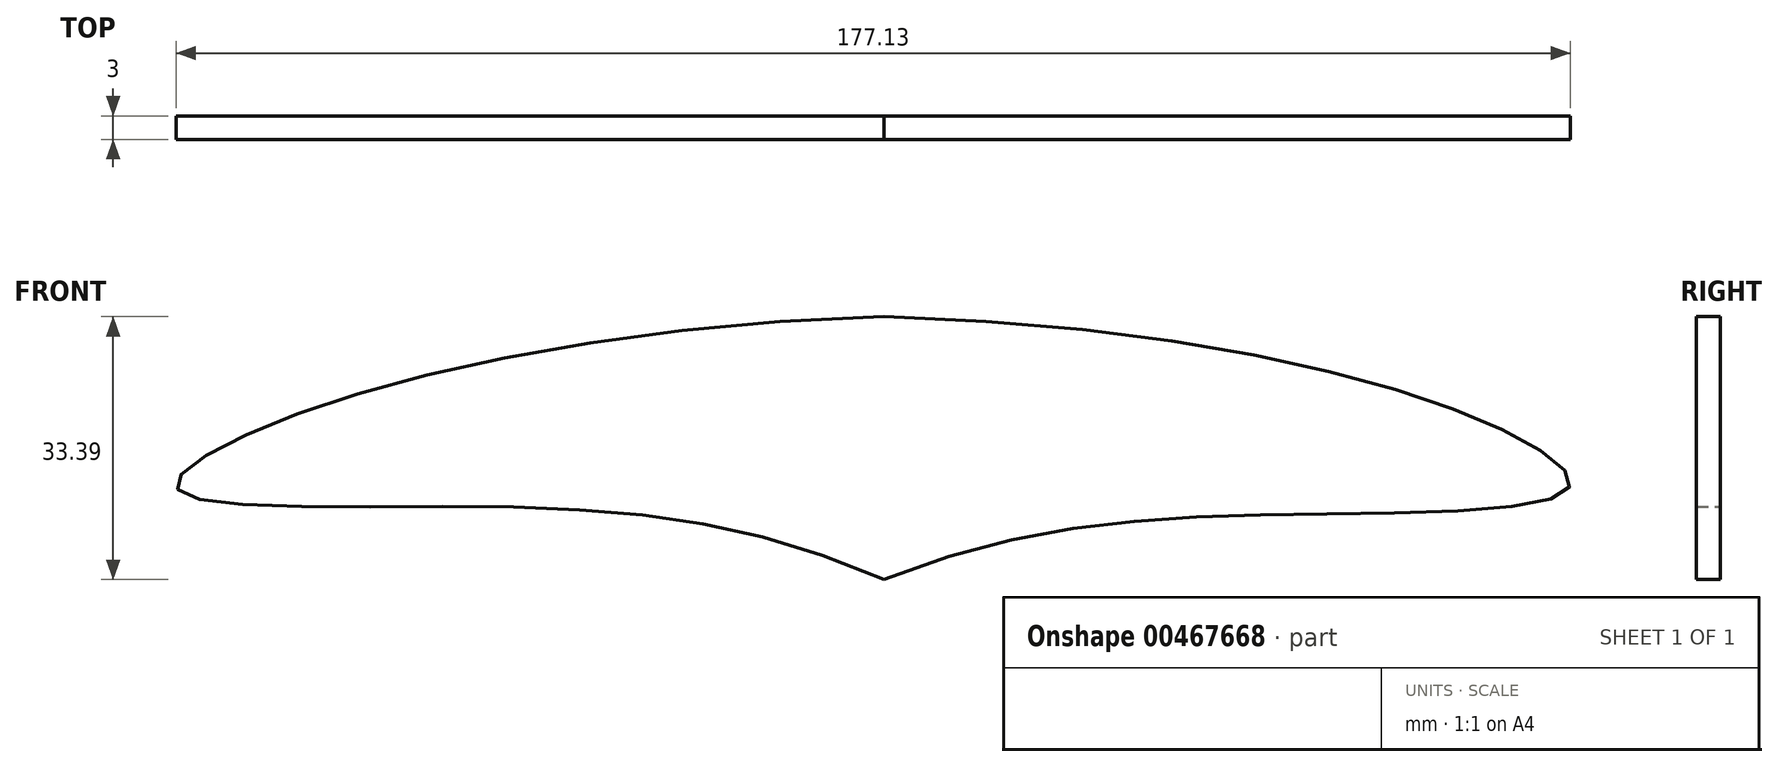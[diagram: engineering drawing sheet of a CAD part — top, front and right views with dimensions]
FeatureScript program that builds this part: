
annotation { "Feature Type Name" : "Feature", "Feature Type Description" : "" }
export const myFeature = defineFeature(function(context is Context, id is Id, definition is map)
    precondition{}
    {
        {
            var Q0;
            Q0=qCreatedBy(makeId("Front.planeOp"),FACE);
            var sketch = newSketch(context, id + "F0", { "sketchPlane" : qUnion([Q0])});
            skFitSpline(sketch, "E0", {"points": [v(0, 21.05) * mm, v(79.22, 6.35) * mm, v(87.03, -0.73) * mm, v(53.27, -4.06) * mm, v(0, -12.34) * mm], "startDerivative": vector(307.3, -8.2) * mm, "endDerivative": vector(-193.41, -77.37) * mm});
            skFitSpline(sketch, "E1", {"points": [v(0, 21.05) * mm, v(-81.9, 5.63) * mm, v(-89.7, -0.9) * mm, v(-50.7, -3.08) * mm, v(0, -12.34) * mm], "startDerivative": vector(-310.28, -8.25) * mm, "endDerivative": vector(182.9, -79.85) * mm});
            skSolve(sketch);
        }
        {
            var Q0;
            Q0 = qSketchRegion(id + "F0", true);
            extrude(context, id + "F1", {"entities" : qUnion([Q0]), "depth" : 3 * mm});
        }
    });
